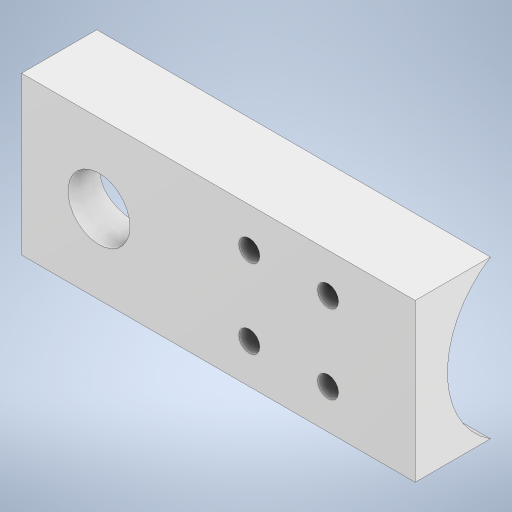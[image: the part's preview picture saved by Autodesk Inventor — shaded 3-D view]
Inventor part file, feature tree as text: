
AUTODESK INVENTOR PART (.ipt)
format: ipt  version: 2023 (Build 270158030, 158C)  size: 271,872 bytes
history: native  units: in
note: dims shown in document units (in); Inventor stores cm internally (conversion verified against a paired STEP export)
features: sketch x4, extrude x3, hole x1, plane x1
ambient origin geometry x8: Origin, YZ Plane, XZ Plane, XY Plane, X Axis, Y Axis, Z Axis, Center Point
bodies: Solid1 (feature_tree)
feature tree (9):
  extrude  "Extrusion1"  Depth=2.0in
  extrude  "Extrusion4"  Depth=0.7874in
  sketch  "Sketch6"  dims[d21=0.0in d22=0.0in]
  hole  "Hole1"  [1 undecoded]
  plane  "Work Plane1"
  extrude  "Extrusion5"  Depth=0.3937in
  sketch  "Sketch1"  dims[d0=2.375in d3=2.0in]
  sketch  "Sketch4"  dims[d4=5.0in d5=0.0in d20=0.7874in]
  sketch  "Sketch7"  dims[d28=0.266in d29=0.2362in d30=0.5906in d31=0.1693in d32=0.5635in d33=0.315in d34=0.8108in d35=1.0in d36=1.0in d38=0.1969in d39=1.0in d40=0.9843in d41=1.0in d42=2.8937in d43=-0.6875in d44=0.4in d45=0.3937in d46=0.0in]
note: 1 required parameter value undecoded (feature->parameter linkage not recoverable at this tier; creation-order binding heuristic only, values carry confidence <= 0.55)
